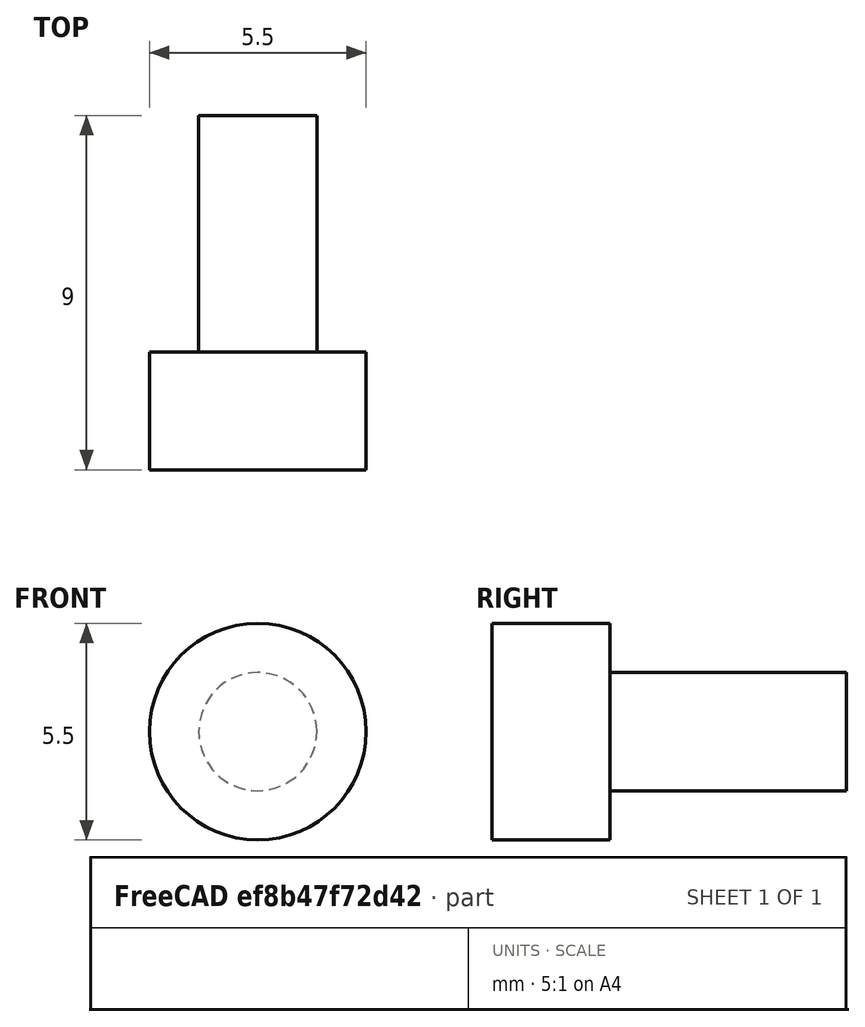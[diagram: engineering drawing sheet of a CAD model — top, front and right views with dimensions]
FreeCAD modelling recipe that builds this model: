
FCSTD DOCUMENT  (FreeCAD 1.0R39319 (Git))
Label: visM3L6
License: All rights reserved
LicenseURL: https://en.wikipedia.org/wiki/All_rights_reserved
objects: Sketcher::SketchObject×1, PartDesign::Revolution×1, PartDesign::Body×1
note: 6 computed .brp shape members not serialized (recipe doc carries the construction recipe); baked Part::Feature solids carry a one-line shape summary decoded from their .brp

FEATURE [Sketcher::SketchObject] Sketch
  ArcFitTolerance = 1e-06
  AttachmentSupport = -> [YZ_Plane]
  FullyConstrained = true
  MakeInternals = false
  MapMode = 5
  Placement = pos=(0,0,0) rot=(0.57735,0.57735,0.57735;2.0944rad)
  sketch-geometry (6):
    g0: LineSegment StartX=-3 StartY=0 StartZ=0 EndX=-3 EndY=2.75 EndZ=0
    g1: LineSegment StartX=-3 StartY=2.75 StartZ=0 EndX=0 EndY=2.75 EndZ=0
    g2: LineSegment StartX=0 StartY=2.75 StartZ=0 EndX=0 EndY=1.5 EndZ=0
    g3: LineSegment StartX=0 StartY=1.5 StartZ=0 EndX=6 EndY=1.5 EndZ=0
    g4: LineSegment StartX=6 StartY=0 StartZ=0 EndX=6 EndY=1.5 EndZ=0
    g5: LineSegment StartX=-3 StartY=0 StartZ=0 EndX=6 EndY=0 EndZ=0
  constraints (18):
    c: PointOnObject(g0,g-1)
    c: Vertical(g0)
    c: Coincident(g1,g0)
    c: PointOnObject(g1,g-2)
    c: Horizontal(g1)
    c: Coincident(g2,g1)
    c: PointOnObject(g2,g-2)
    c: Coincident(g3,g2)
    c: Horizontal(g3)
    c: PointOnObject(g4,g-1)
    c: Coincident(g5,g0)
    c: Coincident(g5,g4)
    c: Coincident(g4,g3)
    c: Perpendicular(g-1,g4)
    c: DistanceY(g0,g0) = 2.75
    c: DistanceX(g1,g1) = 3
    c: DistanceX(g3,g3) = 6
    c: DistanceY(g4,g4) = 1.5
FEATURE [PartDesign::Revolution] Revolution
  Angle = 360
  Angle2 = 60
  Axis = (1e-16,1,-1e-16)
  Base = (0,0,0)
  Placement = pos=(0,0,0) rot=(1,1,1;2.0944rad)
  Profile = -> Sketch
  ReferenceAxis = -> Y_Axis
  Refine = true
  Suppressed = false
  Type = 0
FEATURE [PartDesign::Body] Body  label="Corps"
  AllowCompound = false
  Group = -> [Sketch,Revolution]
  Origin = -> Origin
  Tip = -> Revolution
